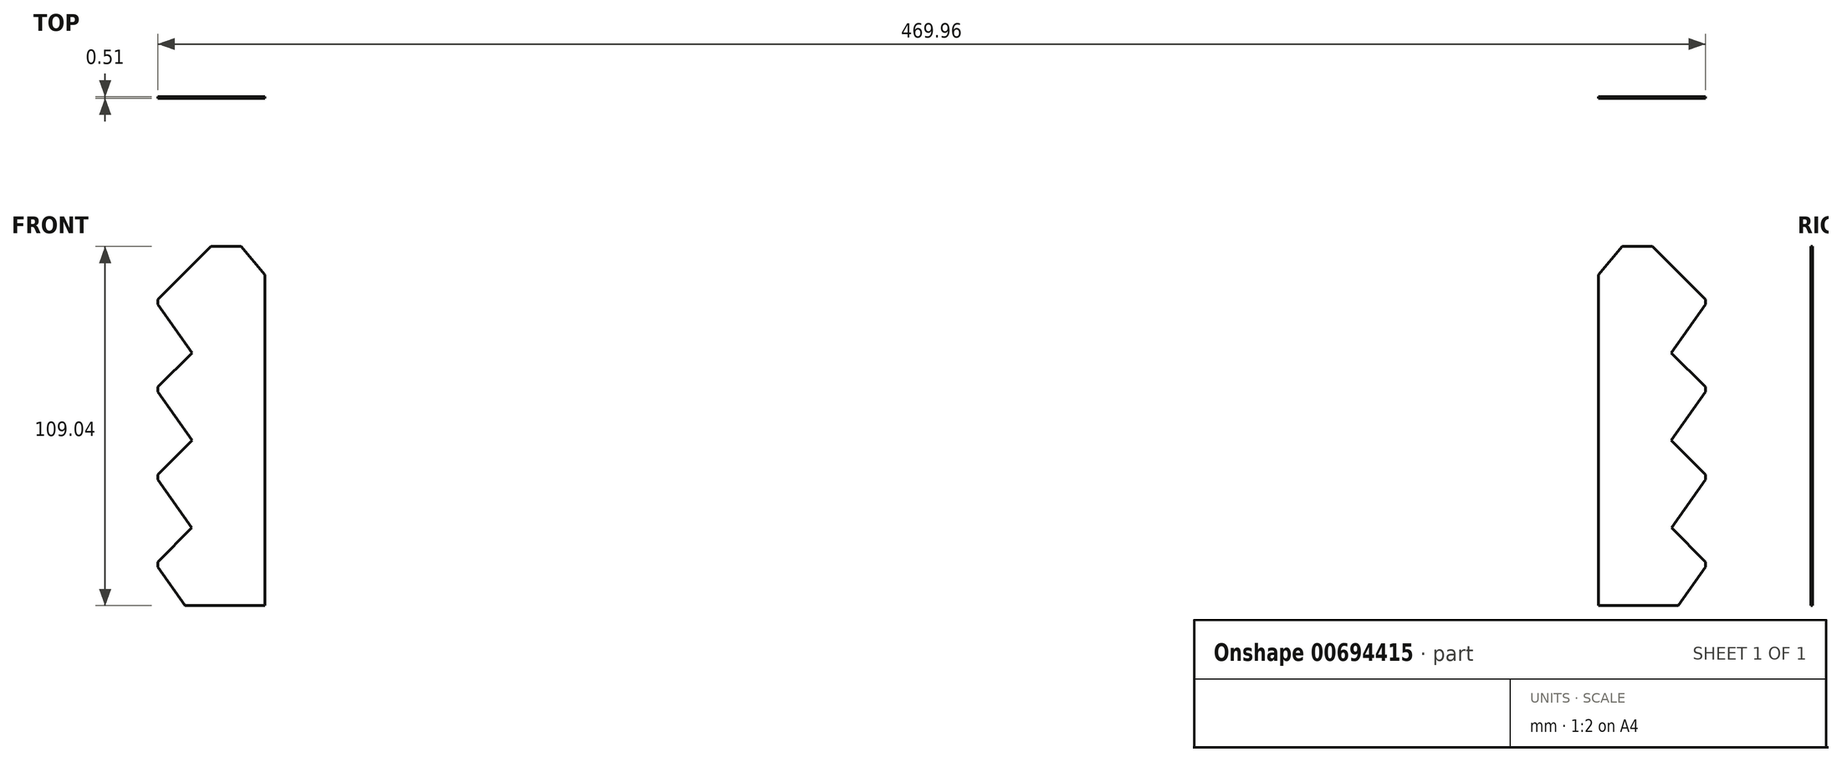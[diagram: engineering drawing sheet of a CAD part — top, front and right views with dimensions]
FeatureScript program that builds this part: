
annotation { "Feature Type Name" : "Feature", "Feature Type Description" : "" }
export const myFeature = defineFeature(function(context is Context, id is Id, definition is map)
    precondition{}
    {
        {
            var Q0;
            Q0=qCreatedBy(makeId("Front.planeOp"),FACE);
            var sketch = newSketch(context, id + "F0", { "sketchPlane" : qUnion([Q0])});
            skLineSegment(sketch, "E0", {"start": v(0, 0) * mm, "end": v(0, 53.04) * mm});
            skLineSegment(sketch, "E1.0", {"start": v(202.47, 0) * mm, "end": v(202.47, 109.04) * mm});
            skPoint(sketch, "E2", {"position": v(170.56, 109.04) * mm});
            skLineSegment(sketch, "E3", {"start": v(202.47, 109.04) * mm, "end": v(244.62, 109.04) * mm});
            skPoint(sketch, "E4", {"position": v(234.98, 118.68) * mm});
            skLineSegment(sketch, "E5", {"start": v(234.98, 118.68) * mm, "end": v(234.98, 11.73) * mm});
            skPoint(sketch, "E6", {"position": v(234.98, 92.99) * mm});
            skLineSegment(sketch, "E7", {"start": v(234.98, 92.99) * mm, "end": v(218.92, 109.04) * mm});
            skPoint(sketch, "E8", {"position": v(234.98, 91.47) * mm});
            skLineSegment(sketch, "E9", {"start": v(234.98, 91.47) * mm, "end": v(224.65, 76.72) * mm});
            skPoint(sketch, "E10", {"position": v(234.98, 66.4) * mm});
            skPoint(sketch, "E11", {"position": v(234.98, 64.87) * mm});
            skPoint(sketch, "E12", {"position": v(234.98, 39.8) * mm});
            skPoint(sketch, "E13", {"position": v(234.98, 38.28) * mm});
            skPoint(sketch, "E14", {"position": v(234.98, 13.26) * mm});
            skPoint(sketch, "E15", {"position": v(234.98, 11.73) * mm});
            skLineSegment(sketch, "E16", {"start": v(234.98, 11.73) * mm, "end": v(226.76, 0) * mm});
            skLineSegment(sketch, "E17", {"start": v(202.47, 0) * mm, "end": v(226.76, 0) * mm});
            skLineSegment(sketch, "E18", {"start": v(234.98, 13.26) * mm, "end": v(224.67, 23.56) * mm});
            skLineSegment(sketch, "E19", {"start": v(234.98, 38.28) * mm, "end": v(224.67, 23.56) * mm});
            skLineSegment(sketch, "E20", {"start": v(234.98, 39.8) * mm, "end": v(224.65, 50.13) * mm});
            skLineSegment(sketch, "E21", {"start": v(234.98, 64.87) * mm, "end": v(224.65, 50.13) * mm});
            skLineSegment(sketch, "E22", {"start": v(234.98, 66.4) * mm, "end": v(224.65, 76.72) * mm});
            skLineSegment(sketch, "E23.0", {"start": v(238.51, 88.99) * mm, "end": v(230.27, 77.21) * mm});
            skLineSegment(sketch, "E24.0", {"start": v(238.03, 69.45) * mm, "end": v(230.27, 77.21) * mm});
            skLineSegment(sketch, "E25.0", {"start": v(238.51, 62.4) * mm, "end": v(230.27, 50.62) * mm});
            skLineSegment(sketch, "E26.0", {"start": v(238.03, 42.86) * mm, "end": v(230.27, 50.62) * mm});
            skLineSegment(sketch, "E27.1", {"start": v(238.51, 35.8) * mm, "end": v(230.29, 24.05) * mm});
            skLineSegment(sketch, "E28.0", {"start": v(238.03, 16.31) * mm, "end": v(230.29, 24.05) * mm});
            skCircle(sketch, "E29", {"center": v(230.27, 77.21) * mm, "radius": 4.32 * mm});
            skCircle(sketch, "E30", {"center": v(230.27, 50.62) * mm, "radius": 4.32 * mm});
            skCircle(sketch, "E31", {"center": v(230.29, 24.05) * mm, "radius": 4.32 * mm});
            skPoint(sketch, "E32", {"position": v(202.47, 100.4) * mm});
            skLineSegment(sketch, "E33", {"start": v(202.47, 100.4) * mm, "end": v(209.72, 109.04) * mm});
            skCircle(sketch, "E34.MirrorC", {"center": v(-230.27, 50.62) * mm, "radius": 4.32 * mm});
            skLineSegment(sketch, "E35.MirrorCS", {"start": v(-238.03, 42.86) * mm, "end": v(-230.27, 50.62) * mm});
            skLineSegment(sketch, "E36.MirrorCS", {"start": v(-238.03, 16.31) * mm, "end": v(-230.29, 24.05) * mm});
            skCircle(sketch, "E37.MirrorC", {"center": v(-230.27, 77.21) * mm, "radius": 4.32 * mm});
            skLineSegment(sketch, "E38.MirrorCS", {"start": v(-234.98, 66.4) * mm, "end": v(-224.65, 76.72) * mm});
            skLineSegment(sketch, "E39.MirrorCS", {"start": v(-234.98, 64.87) * mm, "end": v(-224.65, 50.13) * mm});
            skLineSegment(sketch, "E40.MirrorCS", {"start": v(-238.03, 69.45) * mm, "end": v(-230.27, 77.21) * mm});
            skLineSegment(sketch, "E41.MirrorCS", {"start": v(-234.98, 13.26) * mm, "end": v(-224.67, 23.56) * mm});
            skLineSegment(sketch, "E42.MirrorCS", {"start": v(-238.51, 62.4) * mm, "end": v(-230.27, 50.62) * mm});
            skCircle(sketch, "E43.MirrorC", {"center": v(-230.29, 24.05) * mm, "radius": 4.32 * mm});
            skLineSegment(sketch, "E44.MirrorCS", {"start": v(-234.98, 39.8) * mm, "end": v(-224.65, 50.13) * mm});
            skLineSegment(sketch, "E45.MirrorCS", {"start": v(-234.98, 38.28) * mm, "end": v(-224.67, 23.56) * mm});
            skLineSegment(sketch, "E46.MirrorCS", {"start": v(-238.51, 35.8) * mm, "end": v(-230.29, 24.05) * mm});
            skLineSegment(sketch, "E47.MirrorCS", {"start": v(-202.47, 100.4) * mm, "end": v(-209.72, 109.04) * mm});
            skLineSegment(sketch, "E48.MirrorCS", {"start": v(-234.98, 91.47) * mm, "end": v(-224.65, 76.72) * mm});
            skLineSegment(sketch, "E49.MirrorCS", {"start": v(-238.51, 88.99) * mm, "end": v(-230.27, 77.21) * mm});
            skLineSegment(sketch, "E50.MirrorCS", {"start": v(-234.98, 11.73) * mm, "end": v(-226.76, 0) * mm});
            skPoint(sketch, "E51.MirrorP", {"position": v(-234.98, 39.8) * mm});
            skLineSegment(sketch, "E52.MirrorCS", {"start": v(-234.98, 92.99) * mm, "end": v(-218.92, 109.04) * mm});
            skLineSegment(sketch, "E53.MirrorCS", {"start": v(-234.98, 118.68) * mm, "end": v(-234.98, 11.73) * mm});
            skLineSegment(sketch, "E54.MirrorCS", {"start": v(-202.47, 109.04) * mm, "end": v(-244.62, 109.04) * mm});
            skPoint(sketch, "E55.MirrorP", {"position": v(-234.98, 64.87) * mm});
            skPoint(sketch, "E56.MirrorP", {"position": v(-234.98, 92.99) * mm});
            skPoint(sketch, "E57.MirrorP", {"position": v(-234.98, 91.47) * mm});
            skPoint(sketch, "E58.MirrorP", {"position": v(-234.98, 38.28) * mm});
            skPoint(sketch, "E59.MirrorP", {"position": v(-234.98, 13.26) * mm});
            skLineSegment(sketch, "E60.MirrorCS", {"start": v(-202.47, 0) * mm, "end": v(-226.76, 0) * mm});
            skPoint(sketch, "E61.MirrorP", {"position": v(-234.98, 66.4) * mm});
            skPoint(sketch, "E62.MirrorP", {"position": v(-234.98, 118.68) * mm});
            skPoint(sketch, "E63.MirrorP", {"position": v(-202.47, 100.4) * mm});
            skPoint(sketch, "E64.MirrorP", {"position": v(-170.56, 109.04) * mm});
            skPoint(sketch, "E65.MirrorP", {"position": v(-234.98, 11.73) * mm});
            skLineSegment(sketch, "E66.MirrorCS", {"start": v(-202.47, 0) * mm, "end": v(-202.47, 109.04) * mm});
            skSolve(sketch);
        }
        {
            var Q0;
            {var subQ5=sQuery(id+"F0.wireOp",EDGE,"E7");Q0=makeQuery(id+"F0.imprint","IMPRINT",FACE,{"disambiguationData":[TD([[makeQuery(id+"F0.imprint","IMPRINT",EDGE,{"derivedFrom":subQ5}),1.0]])]});}
            var Q1;
            {var subQ25=sQuery(id+"F0.wireOp",EDGE,"E47.MirrorCS");Q1=makeQuery(id+"F0.imprint","IMPRINT",FACE,{"disambiguationData":[TD([[makeQuery(id+"F0.imprint","IMPRINT",EDGE,{"derivedFrom":subQ25}),1.0]])]});}
            extrude(context, id + "F1", {"entities" : qUnion([Q0, Q1]), "oppositeDirection" : true, "depth" : 0.5 * mm, "offsetDistance" : 25.4 * mm});
        }
    });
